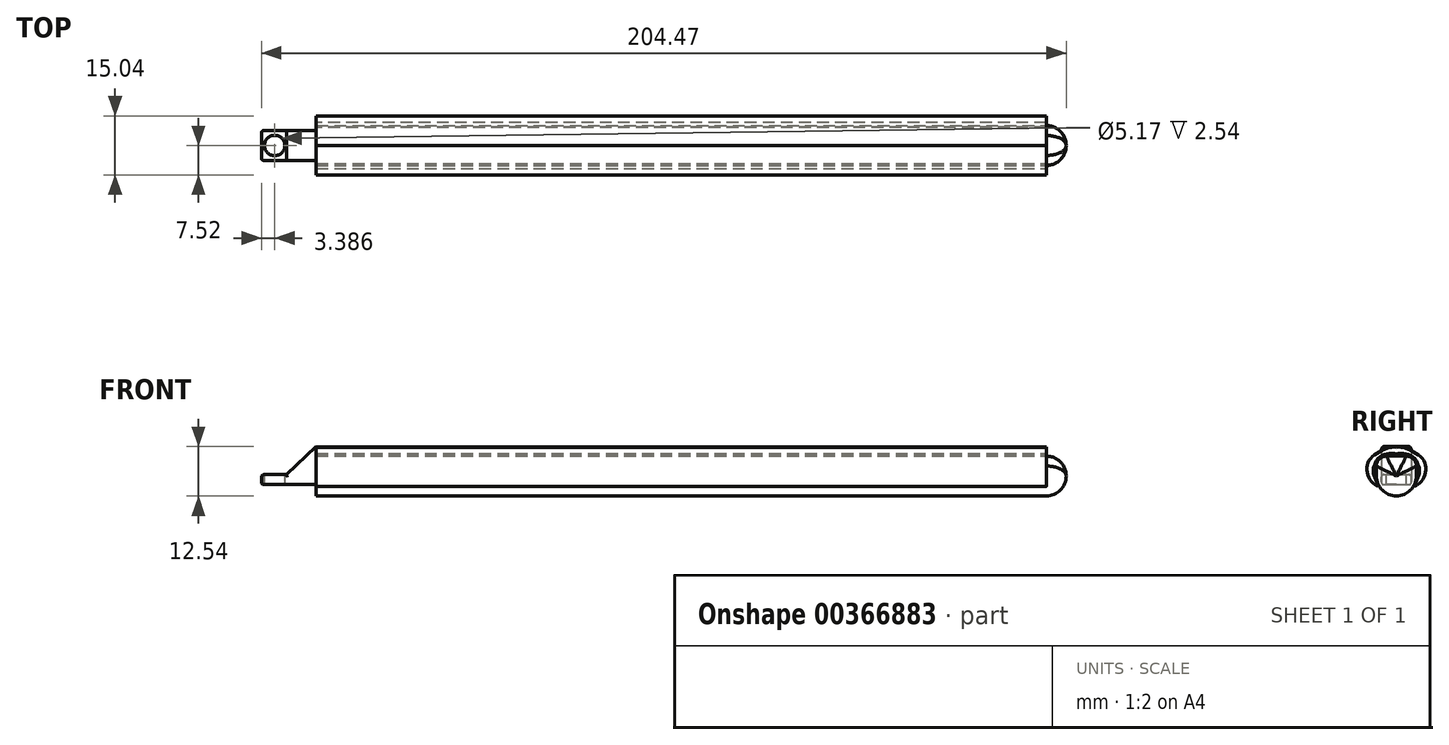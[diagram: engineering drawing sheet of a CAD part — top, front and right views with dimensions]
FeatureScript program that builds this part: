
annotation { "Feature Type Name" : "Feature", "Feature Type Description" : "" }
export const myFeature = defineFeature(function(context is Context, id is Id, definition is map)
    precondition{}
    {
        {
            var Q0;
            Q0=qCreatedBy(makeId("Right.planeOp"),FACE);
            var sketch = newSketch(context, id + "F0", { "sketchPlane" : qUnion([Q0])});
            skLineSegment(sketch, "E0.bottom", {"start": v(2.54, 4.74) * mm, "end": v(-2.54, 4.74) * mm});
            skLineSegment(sketch, "E0.top", {"start": v(0, -5.42) * mm, "end": v(0, -5.42) * mm});
            skLineSegment(sketch, "E0.left", {"start": v(5.08, 2.2) * mm, "end": v(5.08, -0.34) * mm});
            skLineSegment(sketch, "E0.right", {"start": v(-5.08, 2.2) * mm, "end": v(-5.08, -0.34) * mm});
            skPoint(sketch, "E0.middle", {"position": v(0, -0.34) * mm});
            skPoint(sketch, "E1.visualSharp", {"position": v(-5.08, -5.42) * mm});
            skArc(sketch, "E1.filletArc", {"start": v(-5.08, -0.34) * mm, "mid": v(-3.6, -3.93) * mm, "end": v(0, -5.42) * mm});
            skPoint(sketch, "E2.visualSharp", {"position": v(5.08, -5.42) * mm});
            skArc(sketch, "E2.filletArc", {"start": v(0, -5.42) * mm, "mid": v(3.6, -3.93) * mm, "end": v(5.08, -0.34) * mm});
            skPoint(sketch, "E3.visualSharp", {"position": v(-5.08, 4.74) * mm});
            skArc(sketch, "E3.filletArc", {"start": v(-2.54, 4.74) * mm, "mid": v(-4.34, 4) * mm, "end": v(-5.08, 2.2) * mm});
            skPoint(sketch, "E4.visualSharp", {"position": v(5.08, 4.74) * mm});
            skArc(sketch, "E4.filletArc", {"start": v(5.08, 2.2) * mm, "mid": v(4.34, 4) * mm, "end": v(2.54, 4.74) * mm});
            skSolve(sketch);
        }
        {
            var Q0;
            Q0 = qSketchRegion(id + "F0", true);
            extrude(context, id + "F1", {"entities" : qUnion([Q0]), "oppositeDirection" : true, "depth" : 190.5 * mm});
        }
        {
            var Q0;
            Q0=makeQuery(id+"F1.opExtrude","CAP_EDGE",EDGE,{"disambiguationData":[OSD([sQuery(id+"F0.wireOp",EDGE,"E0.bottom")])],"isStart":true});
            fillet(context, id + "F2", {"entities" : qUnion([Q0]), "radius" : 5.08 * mm, "tangentPropagation" : true, "allowEdgeOverflow" : false});
        }
        {
            var Q0;
            Q0=qCreatedBy(makeId("Right.planeOp"),FACE);
            var sketch = newSketch(context, id + "F3", { "sketchPlane" : qUnion([Q0])});
            skFitSpline(sketch, "E5.MirrorCS", {"points": [v(0, 6.96) * mm, v(3.98, 6) * mm, v(7.24, 2.98) * mm, v(6.94, -0.8) * mm, v(4.65, -3) * mm], "startDerivative": vector(14.81, 2.44) * mm, "endDerivative": vector(-11.37, -6.1) * mm});
            skFitSpline(sketch, "E6", {"points": [v(0, 5.3) * mm, v(4.06, 4.67) * mm, v(5.74, 1.84) * mm, v(5.59, -0.54) * mm, v(4.65, -3) * mm, v(5.5, -2.54) * mm], "startDerivative": vector(11.04, 1.48) * mm, "endDerivative": vector(-1.07, -7.96) * mm});
            skFitSpline(sketch, "E7.MirrorCS", {"points": [v(0, 6.96) * mm, v(-3.98, 6) * mm, v(-7.24, 2.98) * mm, v(-6.94, -0.8) * mm, v(-4.65, -3) * mm], "startDerivative": vector(-14.81, 2.44) * mm, "endDerivative": vector(11.37, -6.1) * mm});
            skFitSpline(sketch, "E8.MirrorCS", {"points": [v(0, 5.3) * mm, v(-4.06, 4.67) * mm, v(-5.74, 1.84) * mm, v(-5.59, -0.54) * mm, v(-4.65, -3) * mm, v(-5.5, -2.54) * mm], "startDerivative": vector(-11.04, 1.48) * mm, "endDerivative": vector(1.07, -7.96) * mm});
            skSolve(sketch);
        }
        {
            var Q0;
            Q0 = qSketchRegion(id + "F3", true);
            extrude(context, id + "F4", {"entities" : qUnion([Q0]), "oppositeDirection" : true, "depth" : 190.5 * mm});
        }
        {
            var Q0;
            Q0 = qSketchRegion(id + "F3", true);
            extrude(context, id + "F5", {"entities" : qUnion([Q0]), "operationType" : NewBodyOperationType.REMOVE, "oppositeDirection" : true, "depth" : 5.08 * mm});
        }
        {
            var Q0;
            Q0=qCreatedBy(makeId("Front.planeOp"),FACE);
            var sketch = newSketch(context, id + "F6", { "sketchPlane" : qUnion([Q0])});
            skLineSegment(sketch, "E9", {"start": v(-190.5, -2.54) * mm, "end": v(-198.12, -2.54) * mm});
            skLineSegment(sketch, "E10", {"start": v(-190.5, 7.12) * mm, "end": v(-198.12, 0) * mm});
            skLineSegment(sketch, "E11.bottom", {"start": v(-198.12, -2.54) * mm, "end": v(-204.47, -2.54) * mm});
            skLineSegment(sketch, "E11.top", {"start": v(-198.12, 0) * mm, "end": v(-204.47, 0) * mm});
            skLineSegment(sketch, "E11.left", {"start": v(-198.12, -2.54) * mm, "end": v(-198.12, 0) * mm});
            skLineSegment(sketch, "E11.right", {"start": v(-204.47, -2.54) * mm, "end": v(-204.47, 0) * mm});
            skLineSegment(sketch, "E12", {"start": v(-190.5, 7.12) * mm, "end": v(-190.5, -2.54) * mm});
            skSolve(sketch);
        }
        {
            var Q0;
            Q0 = qSketchRegion(id + "F6", true);
            extrude(context, id + "F7", {"entities" : qUnion([Q0]), "endBound" : BoundingType.SYMMETRIC, "depth" : 7.62 * mm});
        }
        {
            var Q0;
            Q0=makeQuery(id+"F7.opExtrude","CAP_EDGE",EDGE,{"disambiguationData":[OSD([sQuery(id+"F6.wireOp",EDGE,"E10")])],"isStart":true});
            var Q1;
            Q1=makeQuery(id+"F7.opExtrude","CAP_EDGE",EDGE,{"disambiguationData":[OSD([sQuery(id+"F6.wireOp",EDGE,"E10")])],"isStart":false});
            var Q2;
            Q2=makeQuery(id+"F7.opExtrude","CAP_EDGE",EDGE,{"disambiguationData":[OSD([sQuery(id+"F6.wireOp",EDGE,"E11.top")])],"isStart":false});
            var Q3;
            Q3=makeQuery(id+"F7.opExtrude","CAP_EDGE",EDGE,{"disambiguationData":[OSD([sQuery(id+"F6.wireOp",EDGE,"E11.top")])],"isStart":true});
            var Q4;
            Q4=makeQuery(id+"F7.opExtrude","SWEPT_EDGE",EDGE,{"disambiguationData":[OSD([sQuery(id+"F6.wireOp",EDGE,"E11.top"),sQuery(id+"F6.wireOp",EDGE,"E11.right")])]});
            var Q5;
            Q5=makeQuery(id+"F7.opExtrude","CAP_EDGE",EDGE,{"disambiguationData":[OSD([sQuery(id+"F6.wireOp",EDGE,"E9"),sQuery(id+"F6.wireOp",EDGE,"E11.bottom")])],"isStart":false});
            var Q6;
            Q6=makeQuery(id+"F7.opExtrude","CAP_EDGE",EDGE,{"disambiguationData":[OSD([sQuery(id+"F6.wireOp",EDGE,"E11.right")])],"isStart":false});
            var Q7;
            Q7=makeQuery(id+"F7.opExtrude","CAP_EDGE",EDGE,{"disambiguationData":[OSD([sQuery(id+"F6.wireOp",EDGE,"E11.right")])],"isStart":true});
            var Q8;
            Q8=makeQuery(id+"F7.opExtrude","SWEPT_EDGE",EDGE,{"disambiguationData":[OSD([sQuery(id+"F6.wireOp",EDGE,"E11.bottom"),sQuery(id+"F6.wireOp",EDGE,"E11.right")])]});
            var Q9;
            Q9=makeQuery(id+"F7.opExtrude","CAP_EDGE",EDGE,{"disambiguationData":[OSD([sQuery(id+"F6.wireOp",EDGE,"E9"),sQuery(id+"F6.wireOp",EDGE,"E11.bottom")])],"isStart":true});
            fillet(context, id + "F8", {"entities" : qUnion([Q0, Q1, Q2, Q3, Q4, Q5, Q6, Q7, Q8, Q9]), "radius" : 0.64 * mm, "tangentPropagation" : true, "allowEdgeOverflow" : false});
        }
        {
            var Q0;
            Q0=qCreatedBy(makeId("Top.planeOp"),FACE);
            var sketch = newSketch(context, id + "F9", { "sketchPlane" : qUnion([Q0])});
            skCircle(sketch, "E13", {"center": v(-201.08, 0) * mm, "radius": 2.59 * mm});
            skSolve(sketch);
        }
        {
            var Q0;
            Q0 = qSketchRegion(id + "F9", true);
            extrude(context, id + "F10", {"entities" : qUnion([Q0]), "operationType" : NewBodyOperationType.REMOVE, "oppositeDirection" : true, "depth" : 25.4 * mm});
        }
    });
